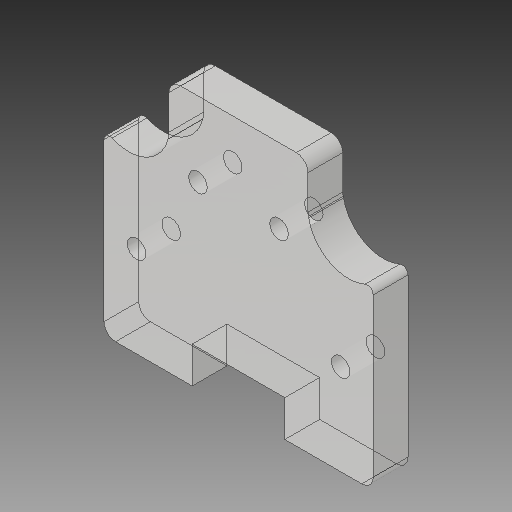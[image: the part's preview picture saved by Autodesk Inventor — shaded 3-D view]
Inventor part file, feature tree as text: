
AUTODESK INVENTOR PART (.ipt)
format: ipt  version: 2017 (Build 210142000, 142)  size: 157,696 bytes
history: native  units: mm
features: sketch x4, other x3, plane x1
ambient origin geometry x8: Origin, YZ Plane, XZ Plane, XY Plane, X Axis, Y Axis, Z Axis, Center Point
bodies: Solid1 (feature_tree)
feature tree (8):
  other  "Hotend Slide Part3.ipt"
  other  "Solid1::Hotend Slide Part3.ipt"
  other  "TaggingFeature1"
  sketch  "Sketch1"  dims[d0=10.0mm]
  sketch  "Sketch2"
  sketch  "Sketch3"
  sketch  "Sketch4"
  plane  "Work Plane1"
